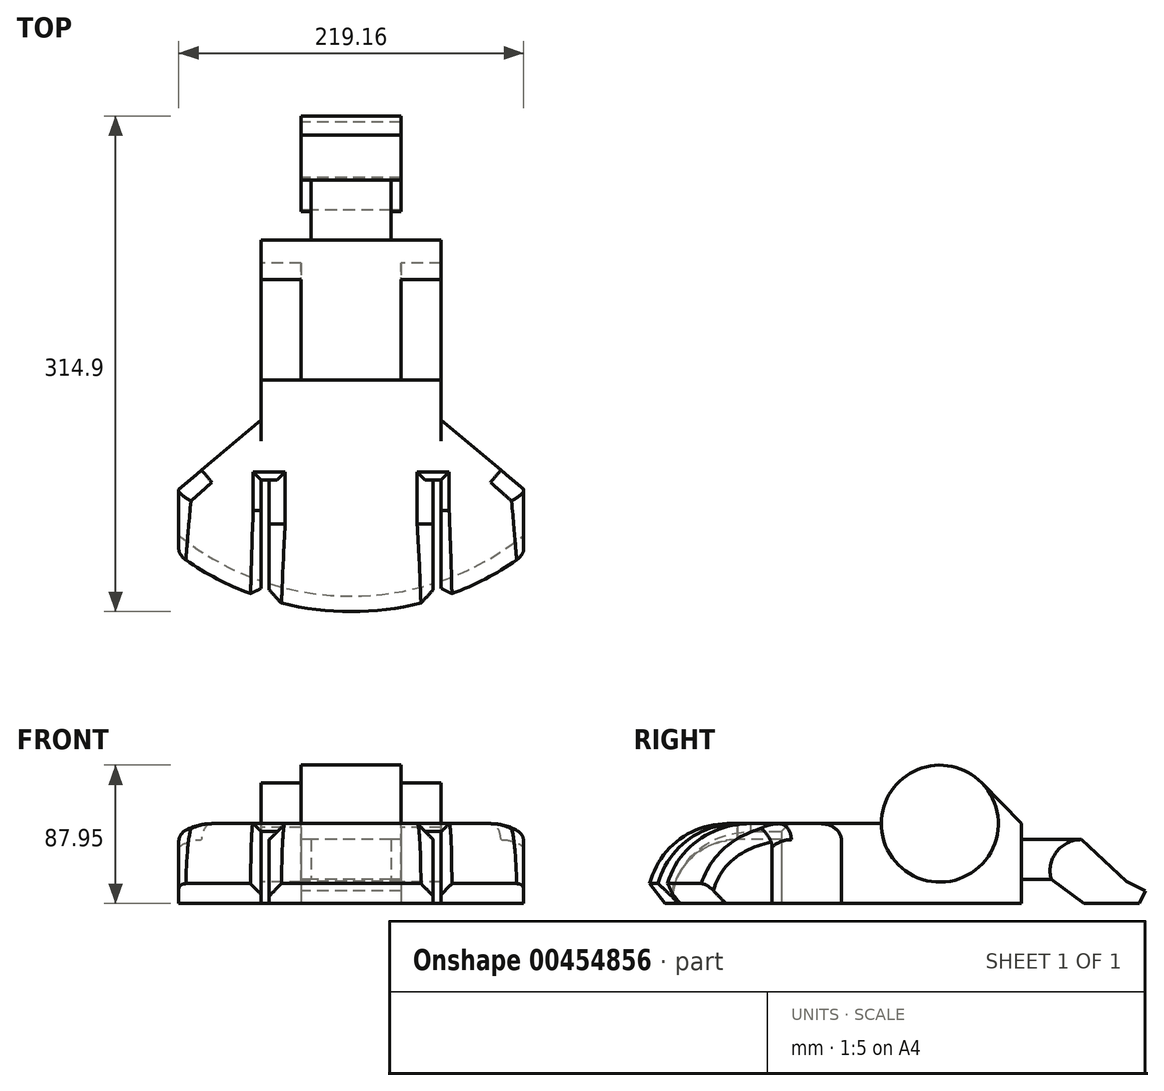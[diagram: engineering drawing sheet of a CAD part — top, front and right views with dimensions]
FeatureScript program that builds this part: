
annotation { "Feature Type Name" : "Feature", "Feature Type Description" : "" }
export const myFeature = defineFeature(function(context is Context, id is Id, definition is map)
    precondition{}
    {
        {
            var Q0;
            Q0=qCreatedBy(makeId("Right.planeOp"),FACE);
            var sketch = newSketch(context, id + "F0", { "sketchPlane" : qUnion([Q0])});
            skLineSegment(sketch, "E0.bottom", {"start": v(76.2, 25.4) * mm, "end": v(-76.2, 25.4) * mm});
            skLineSegment(sketch, "E0.top", {"start": v(76.2, -25.4) * mm, "end": v(-76.2, -25.4) * mm});
            skLineSegment(sketch, "E0.left", {"start": v(76.2, 25.4) * mm, "end": v(76.2, -25.4) * mm});
            skLineSegment(sketch, "E0.right", {"start": v(-76.2, 25.4) * mm, "end": v(-76.2, -25.4) * mm});
            skPoint(sketch, "E0.middle", {"position": v(0, 0) * mm});
            skCircle(sketch, "E1", {"center": v(24.45, 25.4) * mm, "radius": 37.15 * mm});
            skLineSegment(sketch, "E2", {"start": v(76.2, 25.4) * mm, "end": v(51.11, 51.26) * mm});
            skLineSegment(sketch, "E3.bottom", {"start": v(76.2, 15.24) * mm, "end": v(114.3, 15.24) * mm});
            skLineSegment(sketch, "E3.top", {"start": v(76.2, -10.16) * mm, "end": v(114.3, -10.16) * mm});
            skLineSegment(sketch, "E3.left", {"start": v(76.2, 15.24) * mm, "end": v(76.2, -10.16) * mm});
            skLineSegment(sketch, "E3.right", {"start": v(114.3, 15.24) * mm, "end": v(114.3, -10.16) * mm});
            skLineSegment(sketch, "E4", {"start": v(114.3, 2.54) * mm, "end": v(171.32, -25.4) * mm});
            skLineSegment(sketch, "E5", {"start": v(95.25, -10.16) * mm, "end": v(116.05, -25.4) * mm});
            skLineSegment(sketch, "E6", {"start": v(116.05, -25.4) * mm, "end": v(171.32, -25.4) * mm});
            skLineSegment(sketch, "E7", {"start": v(114.3, 15.24) * mm, "end": v(142.81, -11.43) * mm});
            skLineSegment(sketch, "E8", {"start": v(155.12, -17.46) * mm, "end": v(151.23, -25.4) * mm});
            skArc(sketch, "E9", {"start": v(114.3, 15.24) * mm, "mid": v(98.43, 7.3) * mm, "end": v(95.25, -10.16) * mm});
            skLineSegment(sketch, "E10.bottom", {"start": v(-148.94, 25.37) * mm, "end": v(-3.46, 25.37) * mm});
            skLineSegment(sketch, "E10.top", {"start": v(-148.94, -25.37) * mm, "end": v(-3.46, -25.37) * mm});
            skLineSegment(sketch, "E10.left", {"start": v(-148.94, 25.37) * mm, "end": v(-148.94, -25.37) * mm});
            skLineSegment(sketch, "E10.right", {"start": v(-3.46, 25.37) * mm, "end": v(-3.46, -25.37) * mm});
            skPoint(sketch, "E10.middle", {"position": v(-76.2, 0) * mm});
            skSolve(sketch);
        }
        {
            var Q0;
            Q0=makeQuery(id+"F0.imprint","IMPRINT",FACE,{"disambiguationData":[TD([[makeQuery(id+"F0.imprint","IMPRINT",EDGE,{"derivedFrom":sQuery(id+"F0.wireOp",EDGE,"E0.top")}),-1.0]])]});
            var Q1;
            {var subQ0=sQuery(id+"F0.wireOp",EDGE,"E2");Q1=makeQuery(id+"F0.imprint","IMPRINT",FACE,{"disambiguationData":[TD([[makeQuery(id+"F0.imprint","IMPRINT",EDGE,{"derivedFrom":subQ0}),1.0]])]});}
            var Q2;
            {var subQ3=sQuery(id+"F0.wireOp",EDGE,"E0.right");var subQ5=sQuery(id+"F0.wireOp",EDGE,"E10.bottom");var subQ9=makeQuery(id+"F0.imprint","INTERSECT",VERTEX,{"derivedFrom":[subQ3,subQ5]});Q2=makeQuery(id+"F0.imprint","IMPRINT",FACE,{"disambiguationData":[TD([[makeQuery(id+"F0.imprint","IMPRINT",EDGE,{"disambiguationData":[TD([[subQ9,-1.0]])],"derivedFrom":subQ3}),1.0]])]});}
            extrude(context, id + "F1", {"entities" : qUnion([Q0, Q1, Q2]), "endBound" : BoundingType.SYMMETRIC, "depth" : 114.3 * mm, "offsetDistance" : 25.4 * mm});
        }
        {
            var Q0;
            {var subQ0=sQuery(id+"F0.wireOp",EDGE,"E1");var subQ1=sQuery(id+"F0.wireOp",EDGE,"E0.bottom");var subQ2=makeQuery(id+"F0.imprint","INTERSECT",VERTEX,{"disambiguationData":[OD(0.0)],"derivedFrom":[subQ1,subQ0]});Q0=makeQuery(id+"F0.imprint","IMPRINT",FACE,{"disambiguationData":[TD([[makeQuery(id+"F0.imprint","IMPRINT",EDGE,{"disambiguationData":[TD([[subQ2,-1.0]])],"derivedFrom":subQ1}),-1.0]])]});}
            var Q1;
            {var subQ0=sQuery(id+"F0.wireOp",EDGE,"E1");var subQ1=sQuery(id+"F0.wireOp",EDGE,"E0.bottom");var subQ2=makeQuery(id+"F0.imprint","INTERSECT",VERTEX,{"disambiguationData":[OD(0.0)],"derivedFrom":[subQ1,subQ0]});Q1=makeQuery(id+"F0.imprint","IMPRINT",FACE,{"disambiguationData":[TD([[makeQuery(id+"F0.imprint","IMPRINT",EDGE,{"disambiguationData":[TD([[subQ2,-1.0]])],"derivedFrom":subQ1}),1.0]])]});}
            var Q2;
            {var subQ0=sQuery(id+"F0.wireOp",EDGE,"E1");var subQ1=sQuery(id+"F0.wireOp",EDGE,"E0.bottom");var subQ2=makeQuery(id+"F0.imprint","INTERSECT",VERTEX,{"disambiguationData":[OD(0.0)],"derivedFrom":[subQ1,subQ0]});Q2=makeQuery(id+"F0.imprint","IMPRINT",FACE,{"disambiguationData":[TD([[makeQuery(id+"F0.imprint","IMPRINT",EDGE,{"disambiguationData":[TD([[subQ2,1.0]])],"derivedFrom":subQ1}),-1.0]])]});}
            var Q3;
            {var subQ0=sQuery(id+"F0.wireOp",EDGE,"E1");var subQ1=sQuery(id+"F0.wireOp",EDGE,"E0.bottom");var subQ2=makeQuery(id+"F0.imprint","INTERSECT",VERTEX,{"disambiguationData":[OD(0.0)],"derivedFrom":[subQ1,subQ0]});Q3=makeQuery(id+"F0.imprint","IMPRINT",FACE,{"disambiguationData":[TD([[makeQuery(id+"F0.imprint","IMPRINT",EDGE,{"disambiguationData":[TD([[subQ2,1.0]])],"derivedFrom":subQ1}),1.0]])]});}
            var Q4;
            {var subQ0=sQuery(id+"F0.wireOp",EDGE,"E10.bottom");var subQ1=sQuery(id+"F0.wireOp",EDGE,"E1");var subQ2=makeQuery(id+"F0.imprint","INTERSECT",VERTEX,{"derivedFrom":[subQ1,subQ0]});Q4=makeQuery(id+"F0.imprint","IMPRINT",FACE,{"disambiguationData":[TD([[makeQuery(id+"F0.imprint","IMPRINT",EDGE,{"disambiguationData":[TD([[subQ2,-1.0]])],"derivedFrom":subQ1}),1.0]])]});}
            extrude(context, id + "F2", {"entities" : qUnion([Q0, Q1, Q2, Q3, Q4]), "operationType" : NewBodyOperationType.ADD, "endBound" : BoundingType.SYMMETRIC, "depth" : 63.5 * mm, "offsetDistance" : 25.4 * mm});
        }
        {
            var Q0;
            Q0=makeQuery(id+"F0.imprint","IMPRINT",FACE,{"disambiguationData":[TD([[makeQuery(id+"F0.imprint","IMPRINT",EDGE,{"derivedFrom":sQuery(id+"F0.wireOp",EDGE,"E3.bottom")}),-1.0]])]});
            extrude(context, id + "F3", {"entities" : qUnion([Q0]), "operationType" : NewBodyOperationType.ADD, "endBound" : BoundingType.SYMMETRIC, "depth" : 50.8 * mm, "offsetDistance" : 25.4 * mm});
        }
        {
            var Q0;
            {var subQ3=sQuery(id+"F0.wireOp",EDGE,"E9");Q0=makeQuery(id+"F0.imprint","IMPRINT",FACE,{"disambiguationData":[TD([[makeQuery(id+"F0.imprint","IMPRINT",EDGE,{"derivedFrom":subQ3}),1.0]])]});}
            var Q1;
            {var subQ0=sQuery(id+"F0.wireOp",EDGE,"E7");Q1=makeQuery(id+"F0.imprint","IMPRINT",FACE,{"disambiguationData":[TD([[makeQuery(id+"F0.imprint","IMPRINT",EDGE,{"derivedFrom":subQ0}),-1.0]])]});}
            var Q2;
            {var subQ7=sQuery(id+"F0.wireOp",EDGE,"E5");Q2=makeQuery(id+"F0.imprint","IMPRINT",FACE,{"disambiguationData":[TD([[makeQuery(id+"F0.imprint","IMPRINT",EDGE,{"derivedFrom":subQ7}),1.0]])]});}
            extrude(context, id + "F4", {"entities" : qUnion([Q0, Q1, Q2]), "operationType" : NewBodyOperationType.ADD, "endBound" : BoundingType.SYMMETRIC, "depth" : 63.5 * mm, "offsetDistance" : 25.4 * mm});
        }
        {
            var Q0;
            Q0=makeQuery(id+"F1.opExtrude","SWEPT_FACE",FACE,{"disambiguationData":[OSD([sQuery(id+"F0.wireOp",EDGE,"E0.top")])]});
            var sketch = newSketch(context, id + "F5", { "sketchPlane" : qUnion([Q0])});
            skLineSegment(sketch, "E11.bottom", {"start": v(57.15, 0) * mm, "end": v(-57.15, 0) * mm});
            skLineSegment(sketch, "E11.top", {"start": v(57.15, 152.4) * mm, "end": v(52.07, 152.4) * mm});
            skLineSegment(sketch, "E11.left", {"start": v(57.15, 0) * mm, "end": v(57.15, 152.4) * mm});
            skLineSegment(sketch, "E11.right", {"start": v(-57.15, 0) * mm, "end": v(-57.15, 152.4) * mm});
            skPoint(sketch, "E11.middle", {"position": v(0, 76.2) * mm});
            skLineSegment(sketch, "E12", {"start": v(-57.15, 38.1) * mm, "end": v(-109.58, 82.1) * mm});
            skLineSegment(sketch, "E13", {"start": v(57.15, 38.1) * mm, "end": v(109.58, 82.1) * mm});
            skArc(sketch, "E14", {"start": v(109.58, 125.7) * mm, "mid": v(0, 161.4) * mm, "end": v(-109.58, 125.7) * mm});
            skLineSegment(sketch, "E15", {"start": v(52.07, 76.2) * mm, "end": v(52.07, 153.96) * mm});
            skLineSegment(sketch, "E16", {"start": v(-52.07, 76.2) * mm, "end": v(-52.07, 153.96) * mm});
            skLineSegment(sketch, "E17", {"start": v(109.58, 82.1) * mm, "end": v(109.58, 125.7) * mm});
            skLineSegment(sketch, "E18", {"start": v(-109.58, 82.1) * mm, "end": v(-109.58, 125.7) * mm});
            skPoint(sketch, "E19.orphan", {"position": v(-134.98, 103.4) * mm});
            skPoint(sketch, "E20.orphan", {"position": v(134.98, 103.4) * mm});
            skLineSegment(sketch, "E21.trimOffspring", {"start": v(-52.07, 152.4) * mm, "end": v(-57.15, 152.4) * mm});
            skLineSegment(sketch, "E22", {"start": v(-57.15, 12.63) * mm, "end": v(57.15, 12.63) * mm});
            skSolve(sketch);
        }
        {
            var Q0;
            {var subQ3=sQuery(id+"F5.wireOp",EDGE,"E18");Q0=makeQuery(id+"F5.imprint","IMPRINT",FACE,{"disambiguationData":[TD([[makeQuery(id+"F5.imprint","IMPRINT",EDGE,{"derivedFrom":subQ3}),-1.0]])]});}
            var Q1;
            {var subQ3=sQuery(id+"F5.wireOp",EDGE,"E17");Q1=makeQuery(id+"F5.imprint","IMPRINT",FACE,{"disambiguationData":[TD([[makeQuery(id+"F5.imprint","IMPRINT",EDGE,{"derivedFrom":subQ3}),1.0]])]});}
            var Q2;
            {var subQ0=sQuery(id+"F5.wireOp",EDGE,"E15");var subQ2=sQuery(id+"F5.wireOp",EDGE,"E14");var subQ3=makeQuery(id+"F5.imprint","INTERSECT",VERTEX,{"derivedFrom":[subQ2,subQ0]});Q2=makeQuery(id+"F5.imprint","IMPRINT",FACE,{"disambiguationData":[TD([[makeQuery(id+"F5.imprint","IMPRINT",EDGE,{"disambiguationData":[TD([[subQ3,-1.0]])],"derivedFrom":subQ2}),1.0]])]});}
            var Q3;
            {var subQ2=sQuery(id+"F5.wireOp",EDGE,"E22");Q3=makeQuery(id+"F5.imprint","IMPRINT",FACE,{"disambiguationData":[TD([[makeQuery(id+"F5.imprint","IMPRINT",EDGE,{"derivedFrom":subQ2}),1.0]])]});}
            extrude(context, id + "F6", {"entities" : qUnion([Q0, Q1, Q2, Q3]), "operationType" : NewBodyOperationType.ADD, "oppositeDirection" : true, "depth" : 50.8 * mm, "offsetDistance" : 25.4 * mm});
        }
        {
            var Q0;
            Q0=makeQuery(id+"F6.opExtrude","CAP_EDGE",EDGE,{"disambiguationData":[OSD([sQuery(id+"F5.wireOp",EDGE,"E14")])],"isStart":false});
            fillet(context, id + "F7", {"entities" : qUnion([Q0]), "radius" : 50.8 * mm, "tangentPropagation" : true, "allowEdgeOverflow" : false});
        }
        {
            var Q0;
            {var subQ0=sQuery(id+"F5.wireOp",EDGE,"E16");var subQ1=sQuery(id+"F5.wireOp",EDGE,"E15");var subQ2=sQuery(id+"F5.wireOp",EDGE,"E14");var subQ3=sQuery(id+"F0.wireOp",EDGE,"E0.top");Q0=makeQuery(id+"F7.opFillet","BLEND_EDGE",EDGE,{"blendedFrom":[makeQuery(id+"F6.opExtrude","CAP_EDGE",EDGE,{"disambiguationData":[OSD([subQ2]),TDD([makeQuery(id+"F5.imprint","IMPRINT",EDGE,{"disambiguationData":[TD([[makeQuery(id+"F5.imprint","INTERSECT",VERTEX,{"derivedFrom":[subQ2,subQ1]}),-1.0]])],"derivedFrom":subQ2})])],"isStart":false}),makeQuery(id+"F6.boolean.opBoolean","MERGE",FACE,{"derivedFrom":[makeQuery(id+"F1.opExtrude","SWEPT_FACE",FACE,{"disambiguationData":[OSD([subQ3])]}),makeQuery(id+"F6.opExtrude","CAP_FACE",FACE,{"disambiguationData":[OSD([subQ3,sQuery(id+"F0.wireOp",EDGE,"E0.right"),sQuery(id+"F5.wireOp",EDGE,"E11.bottom"),sQuery(id+"F5.wireOp",EDGE,"E11.left"),sQuery(id+"F5.wireOp",EDGE,"E11.right"),sQuery(id+"F5.wireOp",EDGE,"E12"),sQuery(id+"F5.wireOp",EDGE,"E13"),subQ2,subQ1,subQ0,sQuery(id+"F5.wireOp",EDGE,"E17"),sQuery(id+"F5.wireOp",EDGE,"E18")])],"isStart":true})]})],"blendedInto":[makeQuery(id+"F6.boolean.opBoolean","MERGE",FACE,{"derivedFrom":[makeQuery(id+"F1.opExtrude","SWEPT_FACE",FACE,{"disambiguationData":[OSD([subQ3])]}),makeQuery(id+"F6.opExtrude","CAP_FACE",FACE,{"disambiguationData":[OSD([subQ3,sQuery(id+"F0.wireOp",EDGE,"E0.right"),sQuery(id+"F5.wireOp",EDGE,"E11.bottom"),sQuery(id+"F5.wireOp",EDGE,"E11.left"),sQuery(id+"F5.wireOp",EDGE,"E11.right"),sQuery(id+"F5.wireOp",EDGE,"E12"),sQuery(id+"F5.wireOp",EDGE,"E13"),subQ2,subQ1,subQ0,sQuery(id+"F5.wireOp",EDGE,"E17"),sQuery(id+"F5.wireOp",EDGE,"E18")])],"isStart":true})]})]});}
            var Q1;
            {var subQ0=sQuery(id+"F5.wireOp",EDGE,"E18");var subQ1=sQuery(id+"F5.wireOp",EDGE,"E14");var subQ2=sQuery(id+"F5.wireOp",EDGE,"E11.right");var subQ3=sQuery(id+"F0.wireOp",EDGE,"E0.top");Q1=makeQuery(id+"F7.opFillet","BLEND_EDGE",EDGE,{"blendedFrom":[makeQuery(id+"F6.opExtrude","CAP_EDGE",EDGE,{"disambiguationData":[OSD([subQ1]),TDD([makeQuery(id+"F5.imprint","IMPRINT",EDGE,{"disambiguationData":[TD([[makeQuery(id+"F5.imprint","INTERSECT",VERTEX,{"derivedFrom":[subQ1,subQ0]}),1.0]])],"derivedFrom":subQ1})])],"isStart":false}),makeQuery(id+"F6.boolean.opBoolean","MERGE",FACE,{"derivedFrom":[makeQuery(id+"F1.opExtrude","SWEPT_FACE",FACE,{"disambiguationData":[OSD([subQ3])]}),makeQuery(id+"F6.opExtrude","CAP_FACE",FACE,{"disambiguationData":[OSD([subQ3,sQuery(id+"F0.wireOp",EDGE,"E0.right"),sQuery(id+"F5.wireOp",EDGE,"E11.bottom"),sQuery(id+"F5.wireOp",EDGE,"E11.left"),subQ2,sQuery(id+"F5.wireOp",EDGE,"E12"),sQuery(id+"F5.wireOp",EDGE,"E13"),subQ1,sQuery(id+"F5.wireOp",EDGE,"E15"),sQuery(id+"F5.wireOp",EDGE,"E16"),sQuery(id+"F5.wireOp",EDGE,"E17"),subQ0])],"isStart":true})]})],"blendedInto":[makeQuery(id+"F6.boolean.opBoolean","MERGE",FACE,{"derivedFrom":[makeQuery(id+"F1.opExtrude","SWEPT_FACE",FACE,{"disambiguationData":[OSD([subQ3])]}),makeQuery(id+"F6.opExtrude","CAP_FACE",FACE,{"disambiguationData":[OSD([subQ3,sQuery(id+"F0.wireOp",EDGE,"E0.right"),sQuery(id+"F5.wireOp",EDGE,"E11.bottom"),sQuery(id+"F5.wireOp",EDGE,"E11.left"),subQ2,sQuery(id+"F5.wireOp",EDGE,"E12"),sQuery(id+"F5.wireOp",EDGE,"E13"),subQ1,sQuery(id+"F5.wireOp",EDGE,"E15"),sQuery(id+"F5.wireOp",EDGE,"E16"),sQuery(id+"F5.wireOp",EDGE,"E17"),subQ0])],"isStart":true})]})]});}
            var Q2;
            {var subQ0=sQuery(id+"F5.wireOp",EDGE,"E17");var subQ1=sQuery(id+"F5.wireOp",EDGE,"E14");var subQ2=sQuery(id+"F5.wireOp",EDGE,"E11.left");var subQ3=sQuery(id+"F0.wireOp",EDGE,"E0.top");Q2=makeQuery(id+"F7.opFillet","BLEND_EDGE",EDGE,{"blendedFrom":[makeQuery(id+"F6.opExtrude","CAP_EDGE",EDGE,{"disambiguationData":[OSD([subQ1]),TDD([makeQuery(id+"F5.imprint","IMPRINT",EDGE,{"disambiguationData":[TD([[makeQuery(id+"F5.imprint","INTERSECT",VERTEX,{"derivedFrom":[subQ1,subQ0]}),-1.0]])],"derivedFrom":subQ1})])],"isStart":false}),makeQuery(id+"F6.boolean.opBoolean","MERGE",FACE,{"derivedFrom":[makeQuery(id+"F1.opExtrude","SWEPT_FACE",FACE,{"disambiguationData":[OSD([subQ3])]}),makeQuery(id+"F6.opExtrude","CAP_FACE",FACE,{"disambiguationData":[OSD([subQ3,sQuery(id+"F0.wireOp",EDGE,"E0.right"),sQuery(id+"F5.wireOp",EDGE,"E11.bottom"),subQ2,sQuery(id+"F5.wireOp",EDGE,"E11.right"),sQuery(id+"F5.wireOp",EDGE,"E12"),sQuery(id+"F5.wireOp",EDGE,"E13"),subQ1,sQuery(id+"F5.wireOp",EDGE,"E15"),sQuery(id+"F5.wireOp",EDGE,"E16"),subQ0,sQuery(id+"F5.wireOp",EDGE,"E18")])],"isStart":true})]})],"blendedInto":[makeQuery(id+"F6.boolean.opBoolean","MERGE",FACE,{"derivedFrom":[makeQuery(id+"F1.opExtrude","SWEPT_FACE",FACE,{"disambiguationData":[OSD([subQ3])]}),makeQuery(id+"F6.opExtrude","CAP_FACE",FACE,{"disambiguationData":[OSD([subQ3,sQuery(id+"F0.wireOp",EDGE,"E0.right"),sQuery(id+"F5.wireOp",EDGE,"E11.bottom"),subQ2,sQuery(id+"F5.wireOp",EDGE,"E11.right"),sQuery(id+"F5.wireOp",EDGE,"E12"),sQuery(id+"F5.wireOp",EDGE,"E13"),subQ1,sQuery(id+"F5.wireOp",EDGE,"E15"),sQuery(id+"F5.wireOp",EDGE,"E16"),subQ0,sQuery(id+"F5.wireOp",EDGE,"E18")])],"isStart":true})]})]});}
            chamfer(context, id + "F8", {"entities" : qUnion([Q0, Q1, Q2]), "width" : 10.16 * mm, "tangentPropagation" : true});
        }
        {
            var Q0;
            {var subQ0=sQuery(id+"F5.wireOp",EDGE,"E15");var subQ1=sQuery(id+"F5.wireOp",EDGE,"E14");Q0=makeQuery(id+"F7.opFillet","BLEND_EDGE",EDGE,{"blendedFrom":[makeQuery(id+"F6.opExtrude","CAP_EDGE",EDGE,{"disambiguationData":[OSD([subQ1]),TDD([makeQuery(id+"F5.imprint","IMPRINT",EDGE,{"disambiguationData":[TD([[makeQuery(id+"F5.imprint","INTERSECT",VERTEX,{"derivedFrom":[subQ1,subQ0]}),-1.0]])],"derivedFrom":subQ1})])],"isStart":false}),makeQuery(id+"F6.opExtrude","SWEPT_FACE",FACE,{"disambiguationData":[OSD([subQ0])]})],"blendedInto":[makeQuery(id+"F6.opExtrude","SWEPT_FACE",FACE,{"disambiguationData":[OSD([subQ0])]})]});}
            var Q1;
            {var subQ0=sQuery(id+"F5.wireOp",EDGE,"E16");var subQ1=sQuery(id+"F5.wireOp",EDGE,"E14");Q1=makeQuery(id+"F7.opFillet","BLEND_EDGE",EDGE,{"blendedFrom":[makeQuery(id+"F6.opExtrude","CAP_EDGE",EDGE,{"disambiguationData":[OSD([subQ1]),TDD([makeQuery(id+"F5.imprint","IMPRINT",EDGE,{"disambiguationData":[TD([[makeQuery(id+"F5.imprint","INTERSECT",VERTEX,{"derivedFrom":[subQ1,sQuery(id+"F5.wireOp",EDGE,"E15")]}),-1.0]])],"derivedFrom":subQ1})])],"isStart":false}),makeQuery(id+"F6.opExtrude","SWEPT_FACE",FACE,{"disambiguationData":[OSD([subQ0])]})],"blendedInto":[makeQuery(id+"F6.opExtrude","SWEPT_FACE",FACE,{"disambiguationData":[OSD([subQ0])]})]});}
            var Q2;
            Q2=makeQuery(id+"F6.opExtrude","CAP_EDGE",EDGE,{"disambiguationData":[OSD([sQuery(id+"F5.wireOp",EDGE,"E15")])],"isStart":false});
            var Q3;
            Q3=makeQuery(id+"F6.opExtrude","CAP_EDGE",EDGE,{"disambiguationData":[OSD([sQuery(id+"F5.wireOp",EDGE,"E16")])],"isStart":false});
            chamfer(context, id + "F9", {"entities" : qUnion([Q0, Q1, Q2, Q3]), "width" : 10.16 * mm, "tangentPropagation" : true});
        }
        {
            var Q0;
            {var subQ0=sQuery(id+"F0.wireOp",EDGE,"E0.right");var subQ1=sQuery(id+"F0.wireOp",EDGE,"E0.top");var subQ2=makeQuery(id+"F1.opExtrude","SWEPT_EDGE",EDGE,{"disambiguationData":[OSD([subQ1,subQ0])]});Q0=makeQuery(id+"F6.opExtrude","CAP_EDGE",EDGE,{"disambiguationData":[OSD([subQ1,subQ0]),TDD([makeQuery(id+"F5.imprint","IMPRINT",EDGE,{"disambiguationData":[TD([[makeQuery(id+"F5.imprint","INTERSECT",VERTEX,{"derivedFrom":[subQ2,sQuery(id+"F5.wireOp",EDGE,"E11.right")]}),1.0]])],"derivedFrom":subQ2})])],"isStart":false});}
            var Q1;
            {var subQ0=sQuery(id+"F0.wireOp",EDGE,"E0.right");var subQ1=sQuery(id+"F0.wireOp",EDGE,"E0.top");var subQ2=makeQuery(id+"F1.opExtrude","SWEPT_EDGE",EDGE,{"disambiguationData":[OSD([subQ1,subQ0])]});Q1=makeQuery(id+"F6.opExtrude","CAP_EDGE",EDGE,{"disambiguationData":[OSD([subQ1,subQ0]),TDD([makeQuery(id+"F5.imprint","IMPRINT",EDGE,{"disambiguationData":[TD([[makeQuery(id+"F5.imprint","INTERSECT",VERTEX,{"derivedFrom":[subQ2,sQuery(id+"F5.wireOp",EDGE,"E11.left")]}),-1.0]])],"derivedFrom":subQ2})])],"isStart":false});}
            chamfer(context, id + "F10", {"entities" : qUnion([Q0, Q1]), "width" : 5.08 * mm, "tangentPropagation" : true});
        }
        {
            var Q0;
            {var subQ0=sQuery(id+"F5.wireOp",EDGE,"E11.left");Q0=makeQuery(id+"F6.opExtrude","CAP_EDGE",EDGE,{"disambiguationData":[OSD([subQ0]),TDD([makeQuery(id+"F5.imprint","IMPRINT",EDGE,{"disambiguationData":[TD([[makeQuery(id+"F5.imprint","INTERSECT",VERTEX,{"derivedFrom":[makeQuery(id+"F1.opExtrude","SWEPT_EDGE",EDGE,{"disambiguationData":[OSD([sQuery(id+"F0.wireOp",EDGE,"E0.top"),sQuery(id+"F0.wireOp",EDGE,"E0.right")])]}),subQ0]}),-1.0]])],"derivedFrom":subQ0})])],"isStart":false});}
            var Q1;
            {var subQ0=sQuery(id+"F5.wireOp",EDGE,"E11.left");var subQ1=sQuery(id+"F5.wireOp",EDGE,"E14");Q1=makeQuery(id+"F7.opFillet","BLEND_EDGE",EDGE,{"blendedFrom":[makeQuery(id+"F6.opExtrude","CAP_EDGE",EDGE,{"disambiguationData":[OSD([subQ1]),TDD([makeQuery(id+"F5.imprint","IMPRINT",EDGE,{"disambiguationData":[TD([[makeQuery(id+"F5.imprint","INTERSECT",VERTEX,{"derivedFrom":[subQ1,sQuery(id+"F5.wireOp",EDGE,"E17")]}),-1.0]])],"derivedFrom":subQ1})])],"isStart":false}),makeQuery(id+"F6.opExtrude","SWEPT_FACE",FACE,{"disambiguationData":[OSD([subQ0]),TDD([makeQuery(id+"F5.imprint","IMPRINT",EDGE,{"disambiguationData":[TD([[makeQuery(id+"F5.imprint","INTERSECT",VERTEX,{"derivedFrom":[makeQuery(id+"F1.opExtrude","SWEPT_EDGE",EDGE,{"disambiguationData":[OSD([sQuery(id+"F0.wireOp",EDGE,"E0.top"),sQuery(id+"F0.wireOp",EDGE,"E0.right")])]}),subQ0]}),-1.0]])],"derivedFrom":subQ0})])]})],"blendedInto":[makeQuery(id+"F6.opExtrude","SWEPT_FACE",FACE,{"disambiguationData":[OSD([subQ0]),TDD([makeQuery(id+"F5.imprint","IMPRINT",EDGE,{"disambiguationData":[TD([[makeQuery(id+"F5.imprint","INTERSECT",VERTEX,{"derivedFrom":[makeQuery(id+"F1.opExtrude","SWEPT_EDGE",EDGE,{"disambiguationData":[OSD([sQuery(id+"F0.wireOp",EDGE,"E0.top"),sQuery(id+"F0.wireOp",EDGE,"E0.right")])]}),subQ0]}),-1.0]])],"derivedFrom":subQ0})])]})]});}
            var Q2;
            {var subQ0=sQuery(id+"F5.wireOp",EDGE,"E11.right");Q2=makeQuery(id+"F6.opExtrude","CAP_EDGE",EDGE,{"disambiguationData":[OSD([subQ0]),TDD([makeQuery(id+"F5.imprint","IMPRINT",EDGE,{"disambiguationData":[TD([[makeQuery(id+"F5.imprint","INTERSECT",VERTEX,{"derivedFrom":[makeQuery(id+"F1.opExtrude","SWEPT_EDGE",EDGE,{"disambiguationData":[OSD([sQuery(id+"F0.wireOp",EDGE,"E0.top"),sQuery(id+"F0.wireOp",EDGE,"E0.right")])]}),subQ0]}),-1.0]])],"derivedFrom":subQ0})])],"isStart":false});}
            var Q3;
            {var subQ0=sQuery(id+"F5.wireOp",EDGE,"E11.right");var subQ1=sQuery(id+"F5.wireOp",EDGE,"E14");Q3=makeQuery(id+"F7.opFillet","BLEND_EDGE",EDGE,{"blendedFrom":[makeQuery(id+"F6.opExtrude","CAP_EDGE",EDGE,{"disambiguationData":[OSD([subQ1]),TDD([makeQuery(id+"F5.imprint","IMPRINT",EDGE,{"disambiguationData":[TD([[makeQuery(id+"F5.imprint","INTERSECT",VERTEX,{"derivedFrom":[subQ1,sQuery(id+"F5.wireOp",EDGE,"E18")]}),1.0]])],"derivedFrom":subQ1})])],"isStart":false}),makeQuery(id+"F6.opExtrude","SWEPT_FACE",FACE,{"disambiguationData":[OSD([subQ0]),TDD([makeQuery(id+"F5.imprint","IMPRINT",EDGE,{"disambiguationData":[TD([[makeQuery(id+"F5.imprint","INTERSECT",VERTEX,{"derivedFrom":[makeQuery(id+"F1.opExtrude","SWEPT_EDGE",EDGE,{"disambiguationData":[OSD([sQuery(id+"F0.wireOp",EDGE,"E0.top"),sQuery(id+"F0.wireOp",EDGE,"E0.right")])]}),subQ0]}),-1.0]])],"derivedFrom":subQ0})])]})],"blendedInto":[makeQuery(id+"F6.opExtrude","SWEPT_FACE",FACE,{"disambiguationData":[OSD([subQ0]),TDD([makeQuery(id+"F5.imprint","IMPRINT",EDGE,{"disambiguationData":[TD([[makeQuery(id+"F5.imprint","INTERSECT",VERTEX,{"derivedFrom":[makeQuery(id+"F1.opExtrude","SWEPT_EDGE",EDGE,{"disambiguationData":[OSD([sQuery(id+"F0.wireOp",EDGE,"E0.top"),sQuery(id+"F0.wireOp",EDGE,"E0.right")])]}),subQ0]}),-1.0]])],"derivedFrom":subQ0})])]})]});}
            chamfer(context, id + "F11", {"entities" : qUnion([Q0, Q1, Q2, Q3]), "width" : 5.08 * mm, "tangentPropagation" : true});
        }
        {
            var Q0;
            Q0=makeQuery(id+"F6.opExtrude","CAP_EDGE",EDGE,{"disambiguationData":[OSD([sQuery(id+"F5.wireOp",EDGE,"E13")])],"isStart":false});
            var Q1;
            {var subQ0=sQuery(id+"F5.wireOp",EDGE,"E14");Q1=makeQuery(id+"F7.opFillet","BLEND_EDGE",EDGE,{"blendedFrom":[makeQuery(id+"F6.opExtrude","CAP_EDGE",EDGE,{"disambiguationData":[OSD([subQ0]),TDD([makeQuery(id+"F5.imprint","IMPRINT",EDGE,{"disambiguationData":[TD([[makeQuery(id+"F5.imprint","INTERSECT",VERTEX,{"derivedFrom":[subQ0,sQuery(id+"F5.wireOp",EDGE,"E17")]}),-1.0]])],"derivedFrom":subQ0})])],"isStart":false}),makeQuery(id+"F6.opExtrude","SWEPT_FACE",FACE,{"disambiguationData":[OSD([sQuery(id+"F5.wireOp",EDGE,"E13")])]})],"blendedInto":[makeQuery(id+"F6.opExtrude","SWEPT_FACE",FACE,{"disambiguationData":[OSD([sQuery(id+"F5.wireOp",EDGE,"E13")])]})]});}
            var Q2;
            {var subQ0=sQuery(id+"F5.wireOp",EDGE,"E17");var subQ1=sQuery(id+"F5.wireOp",EDGE,"E14");Q2=makeQuery(id+"F7.opFillet","BLEND_EDGE",EDGE,{"blendedFrom":[makeQuery(id+"F6.opExtrude","CAP_EDGE",EDGE,{"disambiguationData":[OSD([subQ1]),TDD([makeQuery(id+"F5.imprint","IMPRINT",EDGE,{"disambiguationData":[TD([[makeQuery(id+"F5.imprint","INTERSECT",VERTEX,{"derivedFrom":[subQ1,subQ0]}),-1.0]])],"derivedFrom":subQ1})])],"isStart":false}),makeQuery(id+"F6.opExtrude","SWEPT_FACE",FACE,{"disambiguationData":[OSD([subQ0])]})],"blendedInto":[makeQuery(id+"F6.opExtrude","SWEPT_FACE",FACE,{"disambiguationData":[OSD([subQ0])]})]});}
            var Q3;
            Q3=makeQuery(id+"F6.opExtrude","CAP_EDGE",EDGE,{"disambiguationData":[OSD([sQuery(id+"F5.wireOp",EDGE,"E12")])],"isStart":false});
            var Q4;
            {var subQ0=sQuery(id+"F5.wireOp",EDGE,"E14");Q4=makeQuery(id+"F7.opFillet","BLEND_EDGE",EDGE,{"blendedFrom":[makeQuery(id+"F6.opExtrude","CAP_EDGE",EDGE,{"disambiguationData":[OSD([subQ0]),TDD([makeQuery(id+"F5.imprint","IMPRINT",EDGE,{"disambiguationData":[TD([[makeQuery(id+"F5.imprint","INTERSECT",VERTEX,{"derivedFrom":[subQ0,sQuery(id+"F5.wireOp",EDGE,"E18")]}),1.0]])],"derivedFrom":subQ0})])],"isStart":false}),makeQuery(id+"F6.opExtrude","SWEPT_FACE",FACE,{"disambiguationData":[OSD([sQuery(id+"F5.wireOp",EDGE,"E12")])]})],"blendedInto":[makeQuery(id+"F6.opExtrude","SWEPT_FACE",FACE,{"disambiguationData":[OSD([sQuery(id+"F5.wireOp",EDGE,"E12")])]})]});}
            var Q5;
            {var subQ0=sQuery(id+"F5.wireOp",EDGE,"E18");var subQ1=sQuery(id+"F5.wireOp",EDGE,"E14");Q5=makeQuery(id+"F7.opFillet","BLEND_EDGE",EDGE,{"blendedFrom":[makeQuery(id+"F6.opExtrude","CAP_EDGE",EDGE,{"disambiguationData":[OSD([subQ1]),TDD([makeQuery(id+"F5.imprint","IMPRINT",EDGE,{"disambiguationData":[TD([[makeQuery(id+"F5.imprint","INTERSECT",VERTEX,{"derivedFrom":[subQ1,subQ0]}),1.0]])],"derivedFrom":subQ1})])],"isStart":false}),makeQuery(id+"F6.opExtrude","SWEPT_FACE",FACE,{"disambiguationData":[OSD([subQ0])]})],"blendedInto":[makeQuery(id+"F6.opExtrude","SWEPT_FACE",FACE,{"disambiguationData":[OSD([subQ0])]})]});}
            fillet(context, id + "F12", {"entities" : qUnion([Q0, Q1, Q2, Q3, Q4, Q5]), "radius" : 10.16 * mm, "tangentPropagation" : true, "allowEdgeOverflow" : false});
        }
    });
